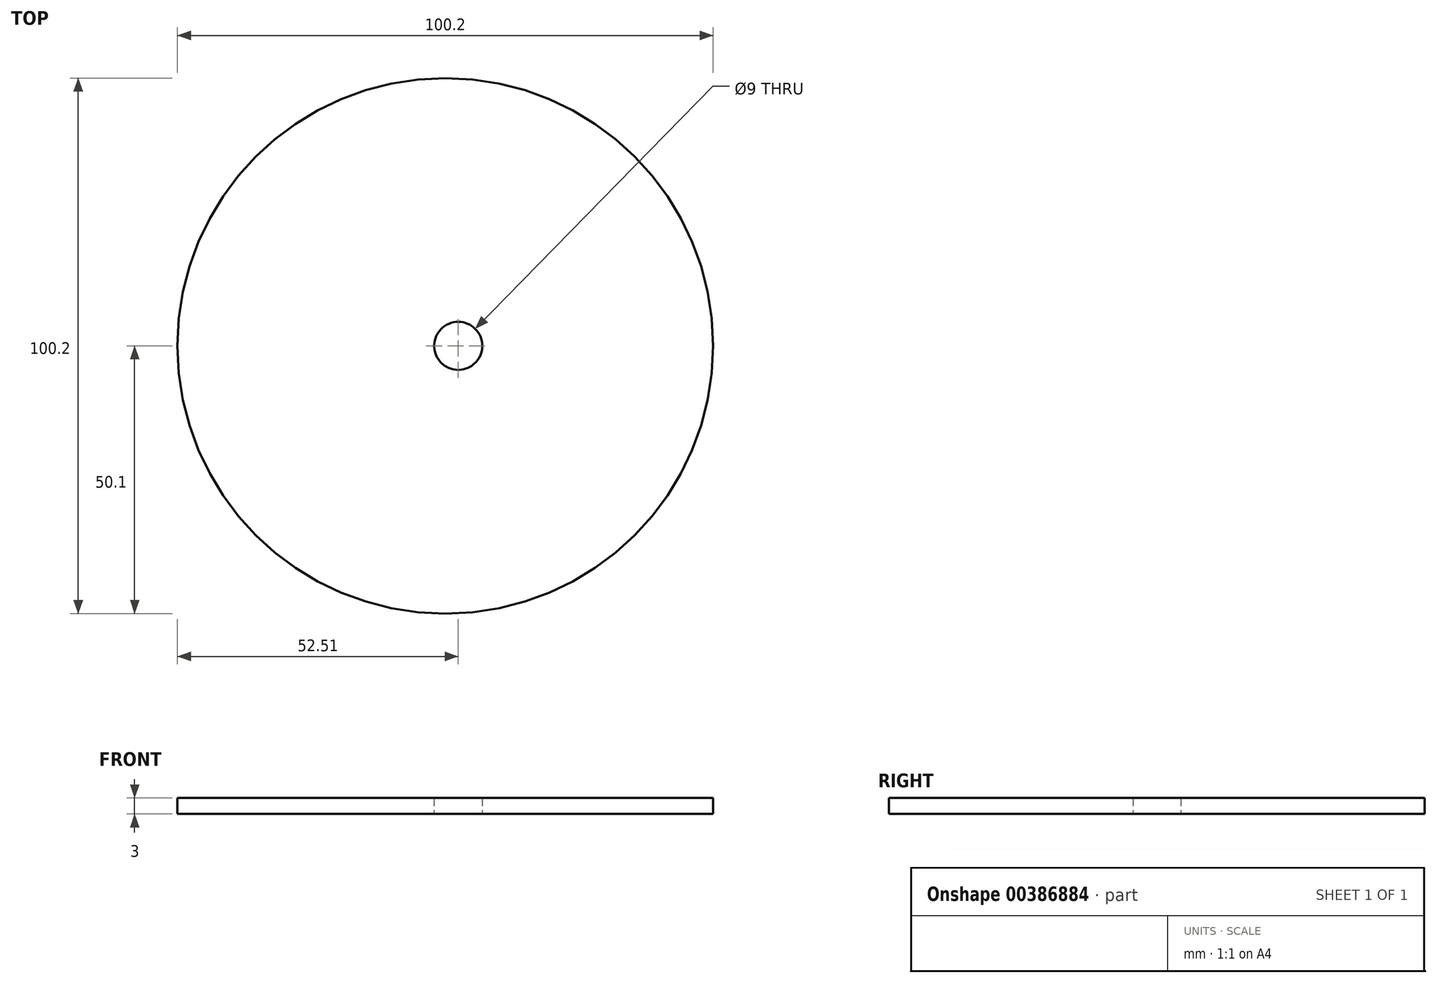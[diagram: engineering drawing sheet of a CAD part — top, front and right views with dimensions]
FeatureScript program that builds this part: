
annotation { "Feature Type Name" : "Feature", "Feature Type Description" : "" }
export const myFeature = defineFeature(function(context is Context, id is Id, definition is map)
    precondition{}
    {
        {
            var Q0;
            Q0=qCreatedBy(makeId("Top.planeOp"),FACE);
            var sketch = newSketch(context, id + "F0", { "sketchPlane" : qUnion([Q0])});
            skCircle(sketch, "E0", {"center": v(-2.41, 0) * mm, "radius": 50.1 * mm});
            skCircle(sketch, "E1", {"center": v(0, 0) * mm, "radius": 4.5 * mm});
            skSolve(sketch);
        }
        {
            var Q0;
            Q0 = qSketchRegion(id + "F0", true);
            extrude(context, id + "F1", {"entities" : qUnion([Q0]), "depth" : 3 * mm});
        }
    });
